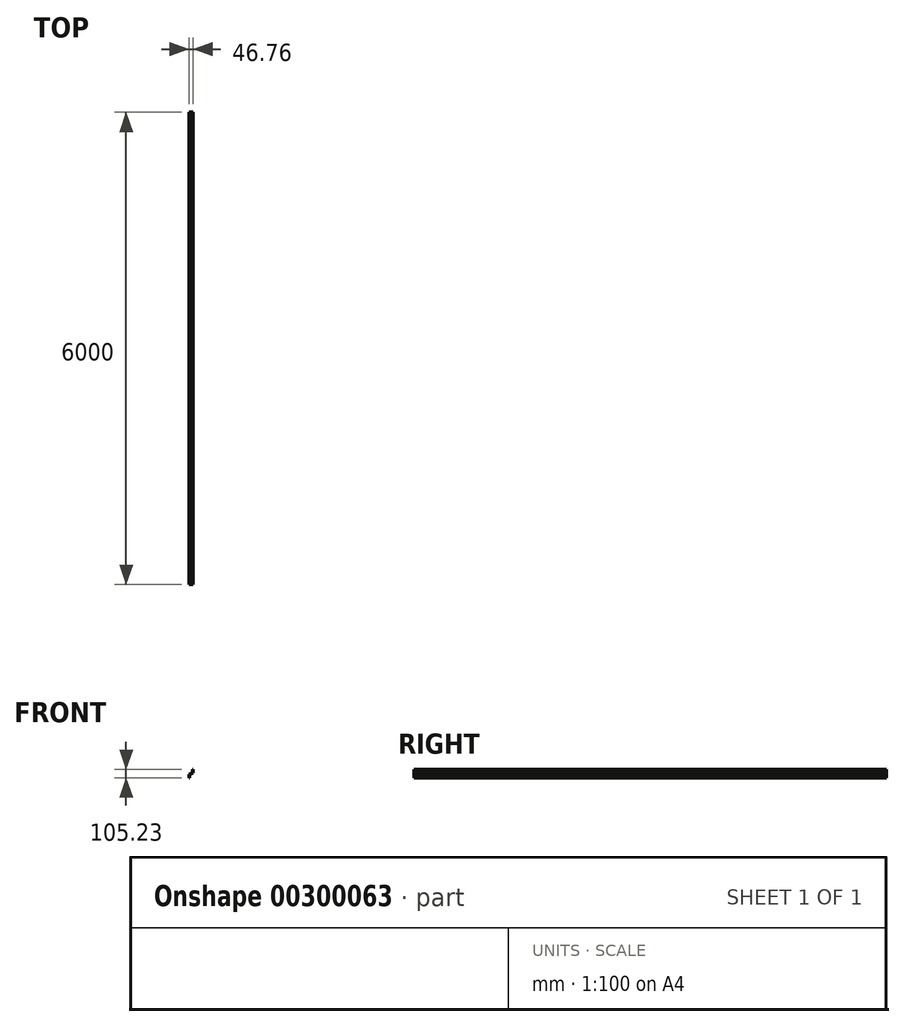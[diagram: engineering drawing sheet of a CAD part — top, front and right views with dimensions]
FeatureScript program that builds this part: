
annotation { "Feature Type Name" : "Feature", "Feature Type Description" : "" }
export const myFeature = defineFeature(function(context is Context, id is Id, definition is map)
    precondition{}
    {
        {
            var Q0;
            Q0=qCreatedBy(makeId("Front.planeOp"),FACE);
            var sketch = newSketch(context, id + "F0", { "sketchPlane" : qUnion([Q0])});
            skLineSegment(sketch, "E0", {"start": v(0, 0) * mm, "end": v(0, -40) * mm});
            skLineSegment(sketch, "E1", {"start": v(0, -40) * mm, "end": v(-43.17, -65.23) * mm});
            skLineSegment(sketch, "E2", {"start": v(-43.17, -65.23) * mm, "end": v(-43.17, -105.23) * mm});
            skLineSegment(sketch, "E3", {"start": v(-43.17, -105.23) * mm, "end": v(-39.17, -105.23) * mm});
            skLineSegment(sketch, "E4", {"start": v(3.59, -42.1) * mm, "end": v(3.59, 0) * mm});
            skLineSegment(sketch, "E5", {"start": v(3.59, 0) * mm, "end": v(0, 0) * mm});
            skLineSegment(sketch, "E6", {"start": v(-39.86, -67.98) * mm, "end": v(3.59, -42.1) * mm});
            skLineSegment(sketch, "E7", {"start": v(-39.86, -67.98) * mm, "end": v(-39.17, -107.43) * mm});
            skSolve(sketch);
        }
        {
            var Q0;
            Q0 = qSketchRegion(id + "F0", true);
            extrude(context, id + "F1", {"entities" : qUnion([Q0]), "depth" : 6000 * mm});
        }
    });
